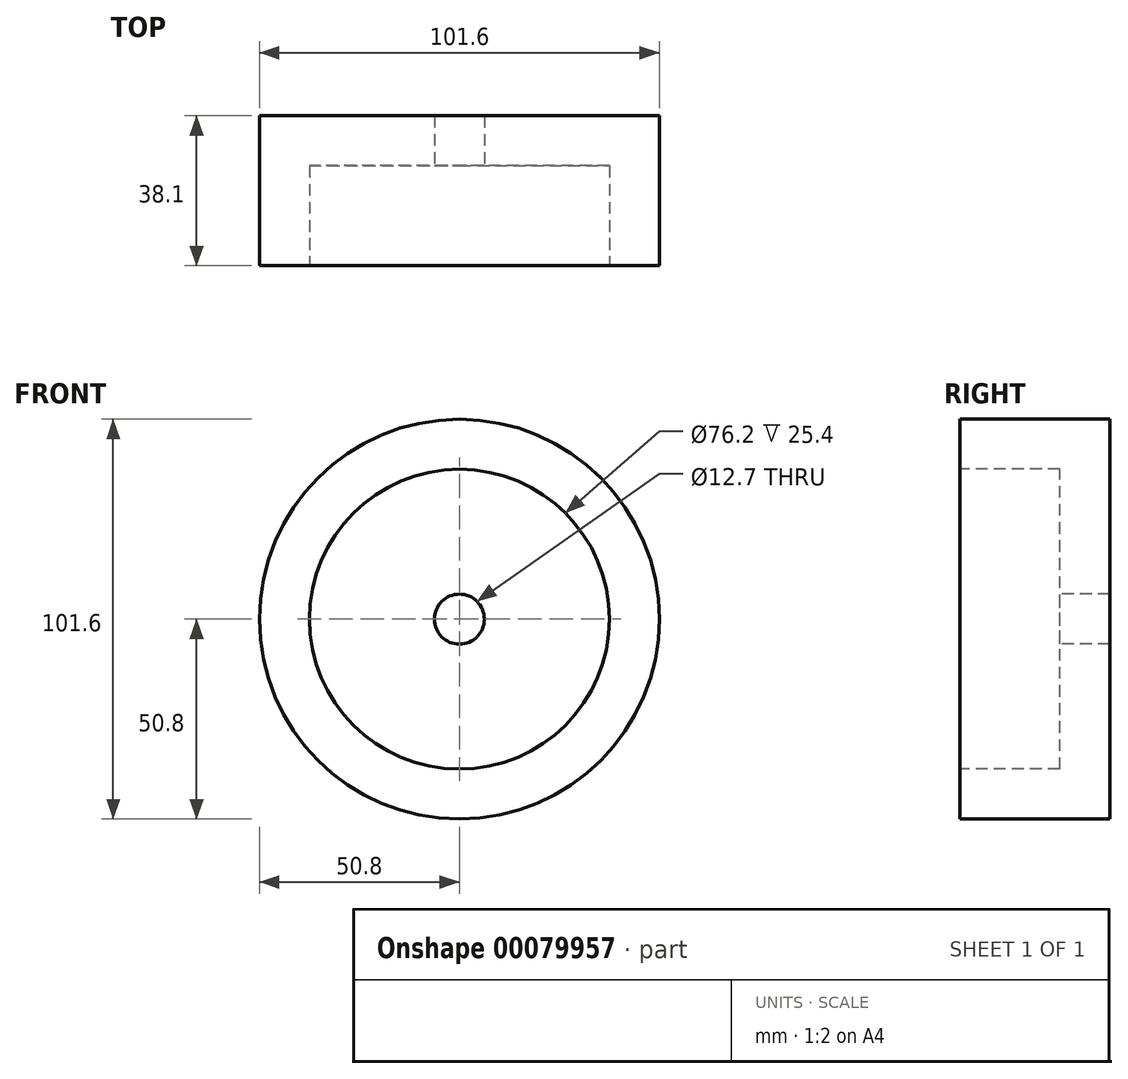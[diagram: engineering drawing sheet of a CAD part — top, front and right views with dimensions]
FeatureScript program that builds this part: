
annotation { "Feature Type Name" : "Feature", "Feature Type Description" : "" }
export const myFeature = defineFeature(function(context is Context, id is Id, definition is map)
    precondition{}
    {
        {
            var Q0;
            Q0=qCreatedBy(makeId("Front.planeOp"),FACE);
            var sketch = newSketch(context, id + "F0", { "sketchPlane" : qUnion([Q0])});
            skCircle(sketch, "E0", {"center": v(0, 0) * mm, "radius": 50.8 * mm});
            skSolve(sketch);
        }
        {
            var Q0;
            Q0 = qSketchRegion(id + "F0", true);
            extrude(context, id + "F1", {"entities" : qUnion([Q0]), "oppositeDirection" : true, "depth" : 38.1 * mm, "offsetDistance" : 25.4 * mm});
        }
        {
            var Q0;
            Q0=makeQuery(id+"F1.opExtrude","CAP_FACE",FACE,{"disambiguationData":[OSD([sQuery(id+"F0.wireOp",EDGE,"E0")])],"isStart":true});
            shell(context, id + "F2", {"entities" : qUnion([Q0]), "thickness" : 12.7 * mm});
        }
        {
            var Q0;
            Q0=qCreatedBy(makeId("Front.planeOp"),FACE);
            var sketch = newSketch(context, id + "F3", { "sketchPlane" : qUnion([Q0])});
            skCircle(sketch, "E1", {"center": v(0, 0) * mm, "radius": 6.35 * mm});
            skSolve(sketch);
        }
        {
            var Q0;
            Q0 = qSketchRegion(id + "F3", true);
            extrude(context, id + "F4", {"entities" : qUnion([Q0]), "operationType" : NewBodyOperationType.REMOVE, "endBound" : BoundingType.THROUGH_ALL, "oppositeDirection" : true, "depth" : 25.4 * mm, "offsetDistance" : 25.4 * mm});
        }
    });
